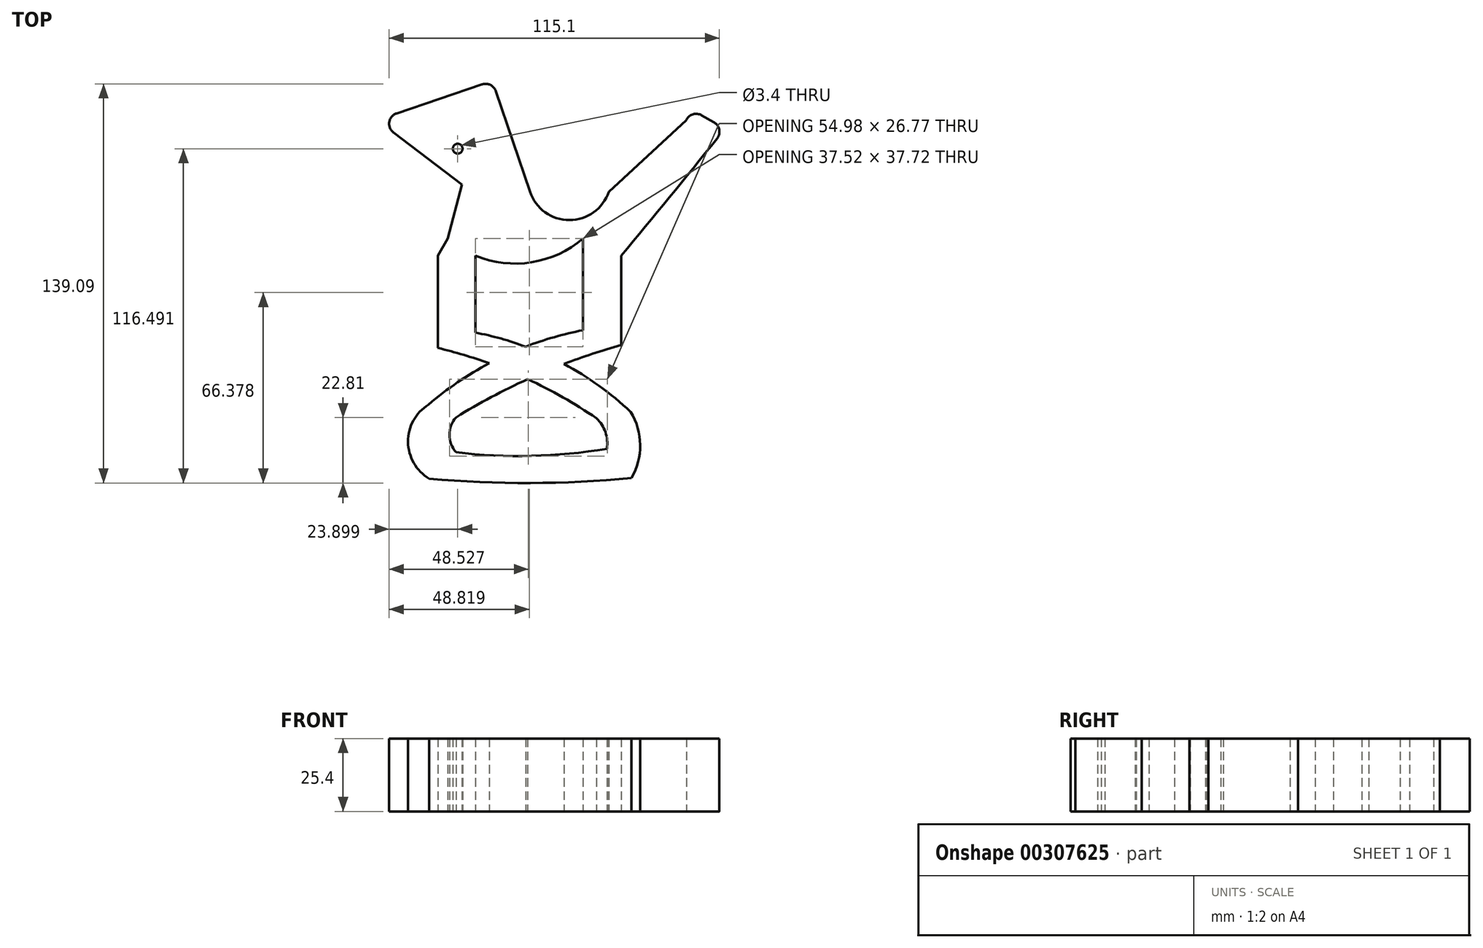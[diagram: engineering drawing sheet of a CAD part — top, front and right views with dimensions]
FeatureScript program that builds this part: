
annotation { "Feature Type Name" : "Feature", "Feature Type Description" : "" }
export const myFeature = defineFeature(function(context is Context, id is Id, definition is map)
    precondition{}
    {
        {
            var Q0;
            Q0=qCreatedBy(makeId("Top.planeOp"),FACE);
            var sketch = newSketch(context, id + "F0", { "sketchPlane" : qUnion([Q0])});
            skLineSegment(sketch, "E0", {"start": v(-60.2, 42.9) * mm, "end": v(-36.33, 24.68) * mm});
            skLineSegment(sketch, "E1", {"start": v(-36.33, 24.68) * mm, "end": v(-41.31, 5.98) * mm});
            skArc(sketch, "E2", {"start": v(-41.31, 5.98) * mm, "mid": v(-17.72, -2.79) * mm, "end": v(5.88, 5.98) * mm});
            skLineSegment(sketch, "E3", {"start": v(5.88, 5.98) * mm, "end": v(19.2, 0) * mm});
            skArc(sketch, "E4", {"start": v(19.2, 0) * mm, "mid": v(35.96, 20.3) * mm, "end": v(52.55, 40.73) * mm});
            skLineSegment(sketch, "E5", {"start": v(51.47, 46.43) * mm, "end": v(47.16, 48.88) * mm});
            skLineSegment(sketch, "E6", {"start": v(41.97, 47.45) * mm, "end": v(41.86, 47.25) * mm});
            skLineSegment(sketch, "E7", {"start": v(-59.11, 49.54) * mm, "end": v(-29.3, 59.63) * mm});
            skPoint(sketch, "E8.visualSharp", {"position": v(-65.89, 47.24) * mm});
            skArc(sketch, "E8.filletArc", {"start": v(-59.11, 49.54) * mm, "mid": v(-61.65, 46.55) * mm, "end": v(-60.2, 42.9) * mm});
            skLineSegment(sketch, "E9", {"start": v(-24.47, 57.25) * mm, "end": v(-12.61, 22.22) * mm});
            skArc(sketch, "E10", {"start": v(-12.61, 22.22) * mm, "mid": v(1.12, 12.38) * mm, "end": v(14.85, 22.22) * mm});
            skLineSegment(sketch, "E11", {"start": v(14.85, 22.22) * mm, "end": v(41.86, 47.25) * mm});
            skPoint(sketch, "E12.visualSharp", {"position": v(-25.7, 60.85) * mm});
            skArc(sketch, "E12.filletArc", {"start": v(-24.47, 57.25) * mm, "mid": v(-26.4, 59.44) * mm, "end": v(-29.3, 59.63) * mm});
            skPoint(sketch, "E13.visualSharp", {"position": v(55.36, 44.22) * mm});
            skArc(sketch, "E13.filletArc", {"start": v(52.55, 40.73) * mm, "mid": v(53.33, 43.83) * mm, "end": v(51.47, 46.43) * mm});
            skPoint(sketch, "E14.visualSharp", {"position": v(43.85, 50.76) * mm});
            skArc(sketch, "E14.filletArc", {"start": v(47.16, 48.88) * mm, "mid": v(44.27, 49.24) * mm, "end": v(41.97, 47.45) * mm});
            skLineSegment(sketch, "E15", {"start": v(41.97, 47.45) * mm, "end": v(52.55, 40.73) * mm});
            skLineSegment(sketch, "E16", {"start": v(49.59, 37.05) * mm, "end": v(38.91, 43.12) * mm});
            skLineSegment(sketch, "E17", {"start": v(38.91, 43.12) * mm, "end": v(41.86, 47.25) * mm});
            skLineSegment(sketch, "E18", {"start": v(-41.31, 5.98) * mm, "end": v(-44.71, 0) * mm});
            skLineSegment(sketch, "E19", {"start": v(-31.64, 0) * mm, "end": v(-31.64, -26.83) * mm});
            skArc(sketch, "E20", {"start": v(22.51, -54.5) * mm, "mid": v(-2.6, -36.81) * mm, "end": v(-31.64, -26.83) * mm});
            skLineSegment(sketch, "E21", {"start": v(-44.71, 0) * mm, "end": v(-44.71, -32.2) * mm});
            skArc(sketch, "E22", {"start": v(10.54, -56.7) * mm, "mid": v(-15.97, -41.92) * mm, "end": v(-44.71, -32.2) * mm});
            skLineSegment(sketch, "E23", {"start": v(5.88, 5.98) * mm, "end": v(5.88, -26) * mm});
            skLineSegment(sketch, "E24", {"start": v(19.2, 0) * mm, "end": v(19.2, -31.21) * mm});
            skArc(sketch, "E25", {"start": v(5.88, -26) * mm, "mid": v(-22.74, -35.48) * mm, "end": v(-48, -51.93) * mm});
            skArc(sketch, "E26", {"start": v(19.2, -31.21) * mm, "mid": v(-10.49, -41.75) * mm, "end": v(-38.4, -56.36) * mm});
            skArc(sketch, "E27", {"start": v(22.76, -77.5) * mm, "mid": v(25.75, -65.97) * mm, "end": v(22.51, -54.5) * mm});
            skArc(sketch, "E28", {"start": v(14.17, -67.32) * mm, "mid": v(13.69, -61.55) * mm, "end": v(10.54, -56.7) * mm});
            skArc(sketch, "E29", {"start": v(-38.4, -56.36) * mm, "mid": v(-40.66, -62.44) * mm, "end": v(-38.4, -68.52) * mm});
            skArc(sketch, "E30", {"start": v(-48, -51.93) * mm, "mid": v(-55.1, -64.91) * mm, "end": v(-47.75, -77.75) * mm});
            skArc(sketch, "E31", {"start": v(-38.4, -68.52) * mm, "mid": v(-12.07, -69.8) * mm, "end": v(14.17, -67.32) * mm});
            skArc(sketch, "E32", {"start": v(-47.75, -77.75) * mm, "mid": v(-12.49, -79.26) * mm, "end": v(22.76, -77.5) * mm});
            skLineSegment(sketch, "E33", {"start": v(-47.32, 33.07) * mm, "end": v(-19.48, 42.5) * mm});
            skLineSegment(sketch, "E34", {"start": v(-19.48, 42.5) * mm, "end": v(-17.92, 37.9) * mm});
            skLineSegment(sketch, "E35", {"start": v(-17.92, 37.9) * mm, "end": v(-42.68, 29.52) * mm});
            skLineSegment(sketch, "E36", {"start": v(45.28, 45.56) * mm, "end": v(41.87, 41.44) * mm});
            skCircle(sketch, "E37", {"center": v(-37.8, 37.23) * mm, "radius": 1.7 * mm});
            skCircle(sketch, "E38", {"center": v(-37.8, 37.23) * mm, "radius": 0.91 * mm});
            skSolve(sketch);
        }
        {
            var Q0;
            Q0 = qSketchRegion(id + "F0", true);
            extrude(context, id + "F1", {"entities" : qUnion([Q0]), "depth" : 25.4 * mm});
        }
    });
